# Revit family: Kohler Taut 74013AR-4ND-CP Family
name_source: partatom
category: Plumbing Fixtures
revit_build: Autodesk Revit 2018 (Build: 20181011_1500(x64)
units: mm (PartAtom-declared; Revit-internal decimal feet)

## family parameters
Cut with Voids When Loaded = No
Host = Face
OmniClass Number = 23.45.55.17
OmniClass Title = Mixing Faucets
Part Type = Normal
Room Calculation Point = No
Round Connector Dimension = Use Diameter
Shared = No

## types (1)
- Kohler Taut 74013AR-4ND-CP
    CW Connection = Yes
    Cold Water Inlet = Cold Water Inlet
    Default Elevation = 914 mm
    Description = Taut®single-handle bathroom sink faucet
    Disclaimer = Although care has been taken to ensure, to the best of our knowledge, that all data and information contained herein is accurate to the extent that it relates to either matters of fact or accepted practice at the time of issue. MDFC (Pty) Ltd assumes no responsibility for any errors in, or misinterpretation of, such data and/ or information or any loss or damage arising from, or related to its use.
    Finish = Metal - Kohler- CP- Polished Chrome
    Flow Rate = 1 GPM
    HW Connection = Yes
    Height = 121 mm
    Hot Water Inlet = Hot Water Inlet
    Length = 144 mm
    Manufacturer = KOHLER Co.
    Material = Brass Construction
    Material main = Brass
    Model = Kohler Taut 74013AR-4ND-CP
    Pressure = 60.00 psi
    Spout Reach = 106 mm
    Telephone = 011 050 9000
    URL = www.africa.kohler.com
    Width = 44 mm

## geometry (parser evidence)
native form markers: Sweep x5
no freeform markers — native parametric forms only
